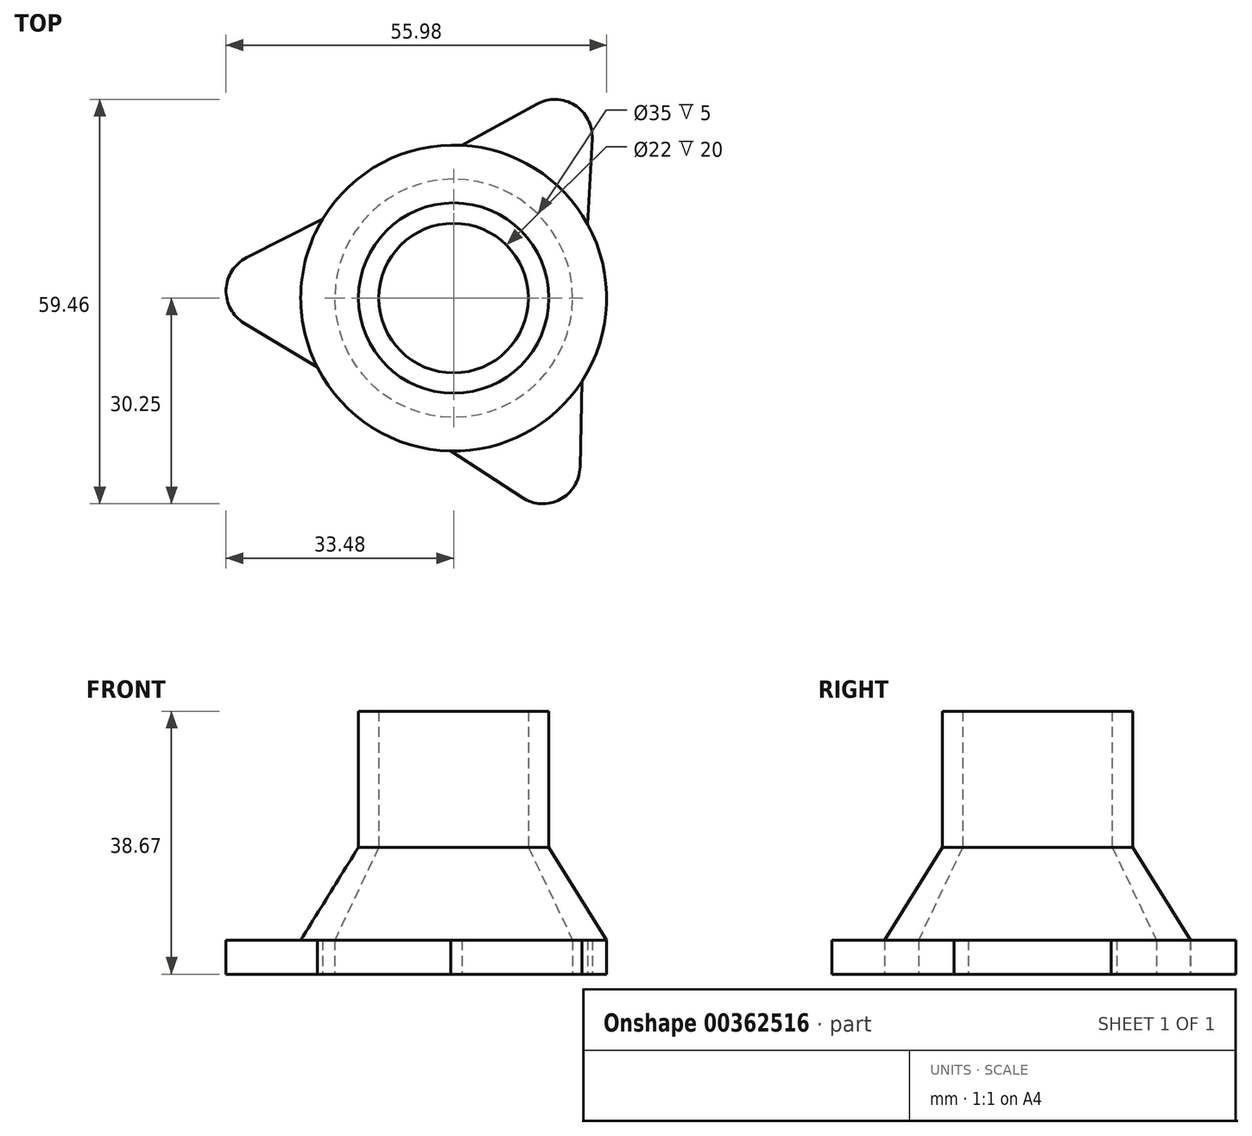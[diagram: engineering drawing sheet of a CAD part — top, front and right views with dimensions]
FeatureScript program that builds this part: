
annotation { "Feature Type Name" : "Feature", "Feature Type Description" : "" }
export const myFeature = defineFeature(function(context is Context, id is Id, definition is map)
    precondition{}
    {
        {
            var Q0;
            Q0=qCreatedBy(makeId("Front.planeOp"),FACE);
            var sketch = newSketch(context, id + "F0", { "sketchPlane" : qUnion([Q0])});
            skLineSegment(sketch, "E0", {"start": v(0, 0) * mm, "end": v(0, 54.65) * mm, "construction": true});
            skLineSegment(sketch, "E1", {"start": v(17.5, 0) * mm, "end": v(17.5, 5) * mm});
            skLineSegment(sketch, "E2", {"start": v(17.5, 5) * mm, "end": v(11, 18.67) * mm});
            skLineSegment(sketch, "E3", {"start": v(11, 18.67) * mm, "end": v(11, 38.67) * mm});
            skLineSegment(sketch, "E4", {"start": v(17.5, 0) * mm, "end": v(22.5, 0) * mm});
            skLineSegment(sketch, "E5", {"start": v(22.5, 0) * mm, "end": v(22.5, 5) * mm});
            skLineSegment(sketch, "E6", {"start": v(22.5, 5) * mm, "end": v(14, 18.67) * mm});
            skLineSegment(sketch, "E7", {"start": v(14, 18.67) * mm, "end": v(14, 38.67) * mm});
            skLineSegment(sketch, "E8", {"start": v(11, 38.67) * mm, "end": v(14, 38.67) * mm});
            skSolve(sketch);
        }
        {
            var Q0;
            Q0 = qSketchRegion(id + "F0", true);
            var Q1;
            Q1=sQuery(id+"F0.wireOp",EDGE,"E0");
            revolve(context, id + "F1", {"surfaceOperationType" : NewSurfaceOperationType.NEW, "entities" : qUnion([Q0]), "axis" : qUnion([Q1]), "revolveType" : RevolveType.FULL});
        }
        {
            var Q0;
            Q0=makeQuery(id+"F1.opRevolve","SWEPT_FACE",FACE,{"disambiguationData":[OSD([sQuery(id+"F0.wireOp",EDGE,"E4")])]});
            var sketch = newSketch(context, id + "F2", { "sketchPlane" : qUnion([Q0])});
            skCircle(sketch, "E9", {"center": v(0, 0) * mm, "radius": 28 * mm, "construction": true});
            skArc(sketch, "E10", {"start": v(-30.83, 3.67) * mm, "mid": v(-33.48, -1.24) * mm, "end": v(-30.47, -5.94) * mm});
            skLineSegment(sketch, "E11", {"start": v(-19.26, -11.64) * mm, "end": v(-30.47, -5.94) * mm});
            skLineSegment(sketch, "E12", {"start": v(0, 0) * mm, "end": v(-27.98, -1.04) * mm, "construction": true});
            skLineSegment(sketch, "E13.MirrorCS", {"start": v(-20.06, 10.19) * mm, "end": v(-30.83, 3.67) * mm});
            skLineSegment(sketch, "E14.1.0", {"start": v(1.21, -22.47) * mm, "end": v(12.24, -28.53) * mm});
            skArc(sketch, "E14.1.1", {"start": v(12.24, -28.53) * mm, "mid": v(17.81, -28.37) * mm, "end": v(20.38, -23.42) * mm});
            skLineSegment(sketch, "E14.1.2", {"start": v(19.7, -10.86) * mm, "end": v(20.38, -23.42) * mm});
            skLineSegment(sketch, "E14.2.0", {"start": v(18.85, 12.28) * mm, "end": v(18.6, 24.86) * mm});
            skArc(sketch, "E14.2.1", {"start": v(18.6, 24.86) * mm, "mid": v(15.67, 29.61) * mm, "end": v(10.1, 29.36) * mm});
            skLineSegment(sketch, "E14.2.2", {"start": v(-0.45, 22.5) * mm, "end": v(10.1, 29.36) * mm});
            skArc(sketch, "E15", {"start": v(-20.06, 10.19) * mm, "mid": v(-22.48, -0.83) * mm, "end": v(-19.26, -11.64) * mm});
            skArc(sketch, "E16", {"start": v(18.85, 12.28) * mm, "mid": v(10.52, 19.89) * mm, "end": v(-0.45, 22.5) * mm});
            skArc(sketch, "E17", {"start": v(19.7, -10.86) * mm, "mid": v(11.96, -19.06) * mm, "end": v(1.21, -22.47) * mm});
            skSolve(sketch);
        }
        {
            var Q0;
            Q0 = qSketchRegion(id + "F2", true);
            extrude(context, id + "F3", {"entities" : qUnion([Q0]), "operationType" : NewBodyOperationType.ADD, "oppositeDirection" : true, "depth" : 5 * mm, "offsetDistance" : 25 * mm});
        }
    });
